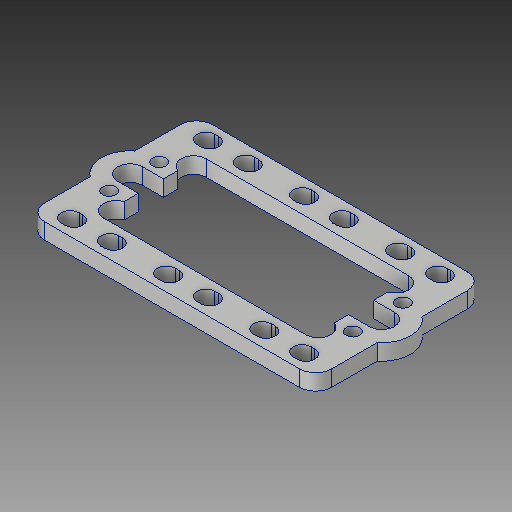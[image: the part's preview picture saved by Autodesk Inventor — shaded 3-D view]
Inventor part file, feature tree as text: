
AUTODESK INVENTOR PART (.ipt)
format: ipt  version: 2019 (Build 230136000, 136)  size: 182,784 bytes
history: native  units: in
note: dims shown in document units (in); Inventor stores cm internally (conversion verified against a paired STEP export)
features: mirror x1
ambient origin geometry x8: Origin, YZ Plane, XZ Plane, XY Plane, X Axis, Y Axis, Z Axis, Center Point
bodies: Solid1 (feature_tree)
feature tree (1):
  mirror  "Mirror2"
